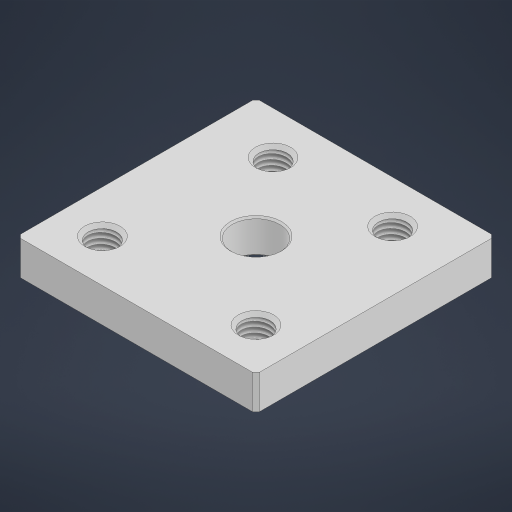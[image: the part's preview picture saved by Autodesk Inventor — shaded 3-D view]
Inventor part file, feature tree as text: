
AUTODESK INVENTOR PART (.ipt)
format: ipt  version: 2024.3 (Build 283343000, 343)  size: 213,504 bytes
history: native  units: mm
features: chamfer x3, sketch x1, extrude x1, hole x1
ambient origin geometry x8: Origin, YZ Plane, XZ Plane, XY Plane, X Axis, Y Axis, Z Axis, Center Point
bodies: Solid1 (feature_tree)
feature tree (6):
  sketch  "Sketch1"  dims[d0=70.0mm d1=45.0mm d2=14.0mm d3=10.0mm d4=0.0mm d5=8.376mm d6=20.0mm d7=4.0mm d8=2.0mm d9=90.0deg d10=7.0mm d11=0.0mm d13=1.0mm d14=2.0mm d15=45.0deg d16=0.5mm d17=2.0mm d18=45.0deg d19=70.0mm d20=35.0mm d21=45.0mm d22=1.0mm d23=2.0mm d24=45.0deg d25=12.5mm d26=17.5mm]
  extrude  "Extrusion1"  Depth=70.0mm
  hole  "Hole1"  [1 undecoded]
  chamfer  "Chamfer1"  Distance=10.0mm
  chamfer  "Chamfer2"  Distance=1.0mm Angle=45.0deg
  chamfer  "Chamfer3"  Distance=0.5mm Angle=45.0deg
note: 1 required parameter value undecoded (feature->parameter linkage not recoverable at this tier; creation-order binding heuristic only, values carry confidence <= 0.55)
